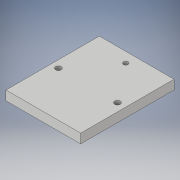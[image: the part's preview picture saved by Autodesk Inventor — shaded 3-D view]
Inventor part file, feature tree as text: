
AUTODESK INVENTOR PART (.ipt)
format: ipt  version: 2019.4 (Build 234330000, 330)  size: 99,840 bytes
history: native  units: in
note: dims shown in document units (in); Inventor stores cm internally (conversion verified against a paired STEP export)
features: sketch x3, hole x2, extrude x1
ambient origin geometry x8: Origin, YZ Plane, XZ Plane, XY Plane, X Axis, Y Axis, Z Axis, Center Point
bodies: Solid1 (feature_tree)
feature tree (6):
  extrude  "Extrusion1"  Depth=3.937in
  hole  "Hole1"  [1 undecoded]
  hole  "Hole2"  [1 undecoded]
  sketch  "Sketch1"  dims[d0=3.1496in d1=3.937in]
  sketch  "Sketch2"  dims[d2=0.3937in d3=0.0in]
  sketch  "Sketch3"  dims[d4=0.1969in d5=0.75in d6=0.375in d7=0.25in d8=0.5635in d9=1.0in d10=0.8108in d11=0.2362in d12=0.75in d13=0.375in d14=0.25in d15=0.5635in d16=1.0in d17=0.8108in]
note: 2 required parameter values undecoded (feature->parameter linkage not recoverable at this tier; creation-order binding heuristic only, values carry confidence <= 0.55)
